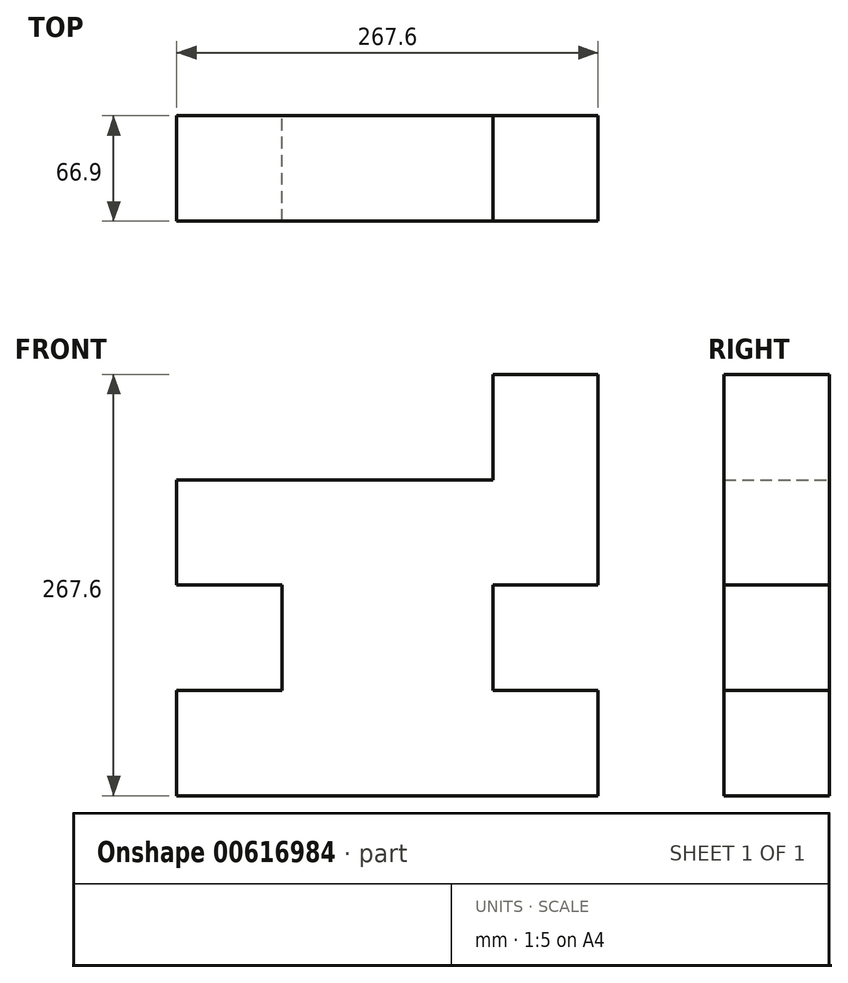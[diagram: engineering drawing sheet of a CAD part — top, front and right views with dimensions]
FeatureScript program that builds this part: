
annotation { "Feature Type Name" : "Feature", "Feature Type Description" : "" }
export const myFeature = defineFeature(function(context is Context, id is Id, definition is map)
    precondition{}
    {
        {
            var Q0;
            Q0=qCreatedBy(makeId("Front.planeOp"),FACE);
            var sketch = newSketch(context, id + "F0", { "sketchPlane" : qUnion([Q0])});
            skLineSegment(sketch, "E0", {"start": v(-152.11, -95.4) * mm, "end": v(115.49, -95.4) * mm});
            skLineSegment(sketch, "E1", {"start": v(115.49, -95.4) * mm, "end": v(115.49, -28.5) * mm});
            skLineSegment(sketch, "E2", {"start": v(115.49, -28.5) * mm, "end": v(48.59, -28.5) * mm});
            skLineSegment(sketch, "E3", {"start": v(48.59, -28.5) * mm, "end": v(48.59, 38.4) * mm});
            skLineSegment(sketch, "E4", {"start": v(48.59, 38.4) * mm, "end": v(115.49, 38.4) * mm});
            skLineSegment(sketch, "E5", {"start": v(115.49, 38.4) * mm, "end": v(115.49, 172.2) * mm});
            skLineSegment(sketch, "E6", {"start": v(115.49, 172.2) * mm, "end": v(48.59, 172.2) * mm});
            skLineSegment(sketch, "E7", {"start": v(48.59, 172.2) * mm, "end": v(48.59, 105.3) * mm});
            skLineSegment(sketch, "E8", {"start": v(48.59, 105.3) * mm, "end": v(-152.11, 105.3) * mm});
            skLineSegment(sketch, "E9", {"start": v(-152.11, 105.3) * mm, "end": v(-152.11, 38.4) * mm});
            skLineSegment(sketch, "E10", {"start": v(-152.11, 38.4) * mm, "end": v(-85.21, 38.4) * mm});
            skLineSegment(sketch, "E11", {"start": v(-85.21, 38.4) * mm, "end": v(-85.21, -28.5) * mm});
            skLineSegment(sketch, "E12", {"start": v(-85.21, -28.5) * mm, "end": v(-152.11, -28.5) * mm});
            skLineSegment(sketch, "E13", {"start": v(-152.11, -28.5) * mm, "end": v(-152.11, -95.4) * mm});
            skSolve(sketch);
        }
        {
            var Q0;
            Q0 = qSketchRegion(id + "F0", true);
            extrude(context, id + "F1", {"entities" : qUnion([Q0]), "depth" : 66.9 * mm, "offsetDistance" : 25 * mm});
        }
    });
